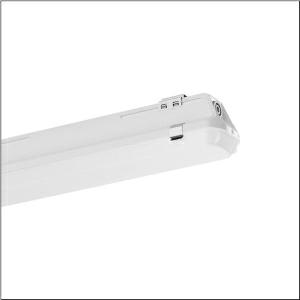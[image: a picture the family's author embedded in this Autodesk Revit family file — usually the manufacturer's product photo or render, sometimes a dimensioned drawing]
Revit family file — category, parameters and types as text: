
# Revit family: monsun_r__11_emergency_51fp20dp467h3h_e354
name_source: partatom
category: Lighting Fixtures
units: mm (PartAtom-declared; Revit-internal decimal feet)

## family parameters
Cut with Voids When Loaded = No
Host = Face
Light Source = No
Part Type = Normal
Room Calculation Point = No
Round Connector Dimension = Use Diameter
Shared = No

## types (1)
- --- (1 x LED, 790 lm, 5 W, 4000K)
    Apparent Load = 5 VA
    CIE Flux Codes = 45 75 93 94 100
    Color Rendering = 80
    Color Temperature = 4000K
    Default Elevation = 1800 mm
    Description = Monsun® 11 emergency, damp-proof luminaire, chain hanger, primary optical cover: enclosure, of PC, light emission: direct distribution, primary light characteristic: symmetric, installation type: suspended mounting, surface-mounted, horizontal mounting, vertical mounting, LED, rated luminous flux: 5.450lm, luminous efficacy: 158lm/W, light colour: 840, colour temperature: 4000K, control gear: ECG DALI, with terminal, 5+3-pole, max. 2.5mm², mains connection: 220..240V, AC, 50/60Hz, rated input power: 35W, control gear: single battery element, battery: NiCd, 4,5Ah, mains connection: 230V, luminaire housing, of glass-fibre reinforced polyester, uncoated, bright grey, incl. chain hanger, length: 1.590mm, width: 90mm, height: 88mm, clip for enclosure, of stainless steel (V2A), ceiling mounting element, of stainless steel (V2A), chain hanger, of stainless steel (V2A), protection rating (complete): IP66, insulation class (complete): insulation class I (protective earthing), certification: CE, UKCA, protection symbol: D, impact resistance: IK08, permissible operating ambient temperature: +5..+35°C, standard: EN 50419, EN 60598-2-1, EN 60598-2-22, no direct snow, no direct sun, no direct rain, for indoor or canopied outdoor use, corresponds to IFS (International Featured Standards) requirements for safety and quality in the food industry, contact your sales advisor before using the luminaires in applications with unclear chemical exposure, large temperature fluctuations or condensation-forming humidity, LABS conformity tested according to VDMA 24364:2018-05, packaging unit: 1 piece
    Height = 89 mm
    Lamp = 1 x LED
    Lamp Light Flux = 790 lm
    Lamp Power = 5 W
    Lamp count = 1
    Length = 1590 mm
    Luminous efficacy = 158 lm/W
    Manufacturer = Siteco
    ModVariant = No
    Model = 51FP20DP467H3H
    Mounting Place = Ceiling
    Mounting Type = Surface mounted
    Number of Poles = 1
    OnlyDefault = Yes
    Power Factor = 1
    Product Name = Monsun® 11 emergency
    Product group = damp-proof luminaire
    ProductGroupID = 301
    Protection Class = Protection class I
    Protection Degree = IP 66
    RLX_Detail_Level = 1
    RLX_Emergency_Light_Flux = 0 lm
    RLX_Emergency_Type = 0
    RLX_Emergency_Type_DB = No
    RlxData = <blob elided: 92489 chars, md5=36ac731d>
    Socket = socket
    Standby Power = 0 W
    System Light Flux = 790 lm
    System Power = 5 W
    Type Comments = : emergency light operation: 3 h
    Type Image = l_1004748.jpg
    URL = http://relux.com
    VarID = @adj_152527
    Voltage = 0 V
    Weight = 0.00 kg
    Width = 90 mm

## geometry (parser evidence)
native form markers: Blend x4, Sweep x14
no freeform markers — native parametric forms only
